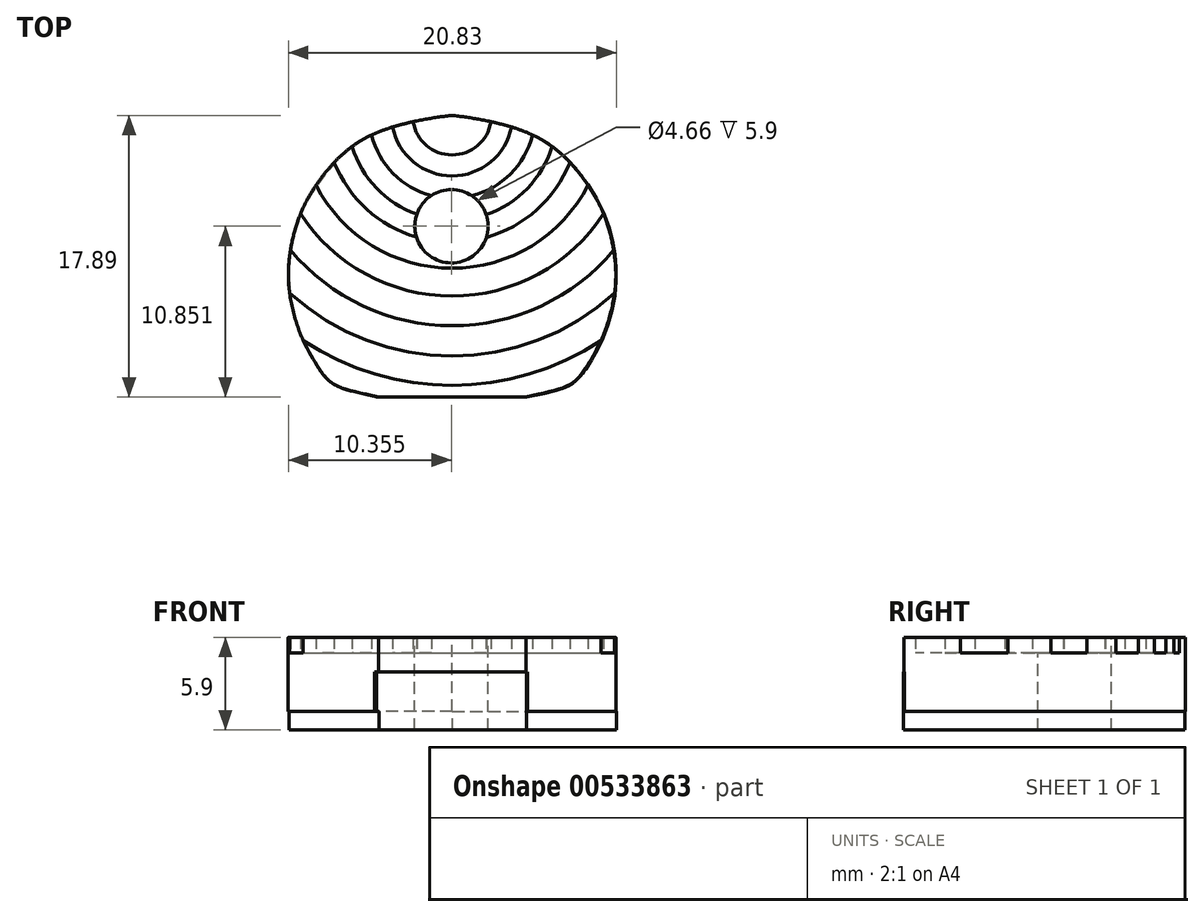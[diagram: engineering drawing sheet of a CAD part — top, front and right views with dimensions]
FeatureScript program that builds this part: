
annotation { "Feature Type Name" : "Feature", "Feature Type Description" : "" }
export const myFeature = defineFeature(function(context is Context, id is Id, definition is map)
    precondition{}
    {
        {
            var Q0;
            Q0=qCreatedBy(makeId("Top.planeOp"),FACE);
            var sketch = newSketch(context, id + "F0", { "sketchPlane" : qUnion([Q0])});
            skLineSegment(sketch, "E0", {"start": v(-18.5, 39.45) * mm, "end": v(-8.99, 39.45) * mm});
            skArc(sketch, "E1", {"start": v(-8.99, 39.45) * mm, "mid": v(-13.75, 56.36) * mm, "end": v(-18.5, 39.45) * mm});
            skLineSegment(sketch, "E2.left", {"start": v(-18.5, 39.45) * mm, "end": v(-18.5, 39.45) * mm});
            skLineSegment(sketch, "E2.right", {"start": v(-8.99, 39.45) * mm, "end": v(-8.99, 39.45) * mm});
            skSolve(sketch);
        }
        {
            var Q0;
            Q0 = qSketchRegion(id + "F0", true);
            extrude(context, id + "F1", {"entities" : qUnion([Q0]), "depth" : 2.5 * mm, "offsetDistance" : 25.4 * mm});
        }
        {
            var Q0;
            Q0=qCreatedBy(makeId("Top.planeOp"),FACE);
            var sketch = newSketch(context, id + "F2", { "sketchPlane" : qUnion([Q0])});
            skCircle(sketch, "E3", {"center": v(-13.67, 50.24) * mm, "radius": 2.3 * mm});
            skSolve(sketch);
        }
        {
            var Q0;
            Q0 = qSketchRegion(id + "F2", true);
            extrude(context, id + "F3", {"entities" : qUnion([Q0]), "operationType" : NewBodyOperationType.REMOVE, "depth" : 25.4 * mm, "offsetDistance" : 25.4 * mm});
        }
        {
            var Q0;
            Q0=qCreatedBy(makeId("Top.planeOp"),FACE);
            var sketch = newSketch(context, id + "F4", { "sketchPlane" : qUnion([Q0])});
            skFitSpline(sketch, "E4", {"points": [v(-13.67, 57.32) * mm, v(-9.2, 56.35) * mm, v(-6.45, 54.6) * mm, v(-4.29, 51.61) * mm, v(-3.41, 48.8) * mm, v(-3.32, 46.28) * mm, v(-4.06, 43.38) * mm, v(-5.02, 41.54) * mm, v(-6.08, 40.3) * mm, v(-8.99, 39.45) * mm], "startDerivative": vector(30, -3) * mm, "endDerivative": vector(-35.55, -8) * mm});
            skFitSpline(sketch, "E5.MirrorCS", {"points": [v(-13.67, 57.32) * mm, v(-18.13, 56.35) * mm, v(-20.9, 54.6) * mm, v(-23.05, 51.61) * mm, v(-23.93, 48.8) * mm, v(-24.02, 46.28) * mm, v(-23.28, 43.38) * mm, v(-22.32, 41.54) * mm, v(-21.26, 40.3) * mm, v(-18.35, 39.45) * mm], "startDerivative": vector(-30, -3) * mm, "endDerivative": vector(35.55, -8) * mm});
            skLineSegment(sketch, "E6", {"start": v(-18.35, 39.45) * mm, "end": v(-8.99, 39.45) * mm});
            skSolve(sketch);
        }
        {
            var Q0;
            Q0 = qSketchRegion(id + "F4", true);
            extrude(context, id + "F5", {"entities" : qUnion([Q0]), "operationType" : NewBodyOperationType.ADD, "oppositeDirection" : true, "depth" : 1.2 * mm, "offsetDistance" : 25.4 * mm});
        }
        {
            var Q0;
            Q0=qCreatedBy(makeId("Top.planeOp"),FACE);
            cPlane(context, id + "F6", {"entities" : qUnion([Q0]), "cplaneType" : CPlaneType.OFFSET, "offset" : 2.5 * mm, "width" : 152.4 * mm, "height" : 152.4 * mm});
        }
        {
            var Q0;
            Q0=qCreatedBy(id+"F6.planeOp",FACE);
            var sketch = newSketch(context, id + "F7", { "sketchPlane" : qUnion([Q0])});
            skFitSpline(sketch, "E7", {"points": [v(-13.7, 57.34) * mm, v(-9.24, 56.37) * mm, v(-6.48, 54.62) * mm, v(-4.32, 51.63) * mm, v(-3.45, 48.83) * mm, v(-3.36, 46.3) * mm, v(-4.1, 43.4) * mm, v(-5.06, 41.56) * mm, v(-6.12, 40.32) * mm, v(-9.02, 39.47) * mm], "startDerivative": vector(30, -3) * mm, "endDerivative": vector(-35.55, -8) * mm});
            skFitSpline(sketch, "E8.MirrorCS", {"points": [v(-13.7, 57.34) * mm, v(-18.17, 56.37) * mm, v(-20.93, 54.62) * mm, v(-23.09, 51.63) * mm, v(-23.96, 48.83) * mm, v(-24.05, 46.3) * mm, v(-23.32, 43.4) * mm, v(-22.35, 41.56) * mm, v(-21.3, 40.32) * mm, v(-18.39, 39.47) * mm], "startDerivative": vector(-30, -3) * mm, "endDerivative": vector(35.55, -8) * mm});
            skLineSegment(sketch, "E9", {"start": v(-18.39, 39.47) * mm, "end": v(-9.02, 39.47) * mm});
            skSolve(sketch);
        }
        {
            var Q0;
            Q0 = qSketchRegion(id + "F7", true);
            extrude(context, id + "F8", {"entities" : qUnion([Q0]), "operationType" : NewBodyOperationType.ADD, "oppositeDirection" : true, "depth" : 2.5 * mm, "offsetDistance" : 25.4 * mm});
        }
        {
            var Q0;
            Q0 = qSketchRegion(id + "F7", true);
            extrude(context, id + "F9", {"entities" : qUnion([Q0]), "operationType" : NewBodyOperationType.ADD, "depth" : 1.2 * mm, "offsetDistance" : 25.4 * mm});
        }
        {
            var Q0;
            Q0=makeQuery(id+"F9.opExtrude","CAP_FACE",FACE,{"disambiguationData":[OSD([sQuery(id+"F7.wireOp",EDGE,"E7"),sQuery(id+"F7.wireOp",EDGE,"E8.MirrorCS"),sQuery(id+"F7.wireOp",EDGE,"E9")])],"isStart":false});
            var sketch = newSketch(context, id + "F10", { "sketchPlane" : qUnion([Q0])});
            skCircle(sketch, "E10", {"center": v(-13.75, 50.3) * mm, "radius": 2.33 * mm});
            skSolve(sketch);
        }
        {
            var Q0;
            Q0 = qSketchRegion(id + "F10", true);
            extrude(context, id + "F11", {"entities" : qUnion([Q0]), "operationType" : NewBodyOperationType.REMOVE, "oppositeDirection" : true, "depth" : 25.4 * mm, "offsetDistance" : 25.4 * mm});
        }
        {
            var Q0;
            Q0=makeQuery(id+"F9.opExtrude","CAP_FACE",FACE,{"disambiguationData":[OSD([sQuery(id+"F7.wireOp",EDGE,"E7"),sQuery(id+"F7.wireOp",EDGE,"E8.MirrorCS"),sQuery(id+"F7.wireOp",EDGE,"E9")])],"isStart":false});
            var sketch = newSketch(context, id + "F12", { "sketchPlane" : qUnion([Q0])});
            skCircle(sketch, "E11", {"center": v(-13.7, 57.34) * mm, "radius": 2.5 * mm});
            skCircle(sketch, "E12", {"center": v(-13.7, 57.34) * mm, "radius": 3.84 * mm});
            skCircle(sketch, "E13", {"center": v(-13.7, 57.34) * mm, "radius": 5.25 * mm});
            skCircle(sketch, "E14", {"center": v(-13.7, 57.34) * mm, "radius": 6.66 * mm});
            skCircle(sketch, "E15", {"center": v(-13.7, 57.34) * mm, "radius": 8.05 * mm});
            skCircle(sketch, "E16", {"center": v(-13.7, 57.34) * mm, "radius": 9.7 * mm});
            skCircle(sketch, "E17", {"center": v(-13.7, 57.34) * mm, "radius": 11.47 * mm});
            skCircle(sketch, "E18", {"center": v(-13.7, 57.34) * mm, "radius": 13.36 * mm});
            skCircle(sketch, "E19", {"center": v(-13.7, 57.34) * mm, "radius": 15.28 * mm});
            skCircle(sketch, "E20", {"center": v(-13.7, 57.34) * mm, "radius": 17.14 * mm});
            skSolve(sketch);
        }
        {
            var Q0;
            {var subQ0=sQuery(id+"F12.wireOp",EDGE,"E11");var subQ1=makeQuery(id+"F9.opExtrude","CAP_EDGE",EDGE,{"disambiguationData":[OSD([sQuery(id+"F7.wireOp",EDGE,"E7")])],"isStart":false});var subQ2=makeQuery(id+"F12.imprint","INTERSECT",VERTEX,{"derivedFrom":[subQ1,subQ0]});Q0=makeQuery(id+"F12.imprint","IMPRINT",FACE,{"disambiguationData":[TD([[makeQuery(id+"F12.imprint","IMPRINT",EDGE,{"disambiguationData":[TD([[subQ2,1.0]])],"derivedFrom":subQ0}),1.0]])]});}
            var Q1;
            {var subQ1=makeQuery(id+"F9.opExtrude","CAP_EDGE",EDGE,{"disambiguationData":[OSD([sQuery(id+"F7.wireOp",EDGE,"E7")])],"isStart":false});var subQ3=sQuery(id+"F12.wireOp",EDGE,"E12");var subQ4=makeQuery(id+"F12.imprint","INTERSECT",VERTEX,{"derivedFrom":[subQ1,subQ3]});Q1=makeQuery(id+"F12.imprint","IMPRINT",FACE,{"disambiguationData":[TD([[makeQuery(id+"F12.imprint","IMPRINT",EDGE,{"disambiguationData":[TD([[subQ4,1.0]])],"derivedFrom":subQ3}),-1.0]])]});}
            var Q2;
            {var subQ0=sQuery(id+"F12.wireOp",EDGE,"E14");var subQ1=makeQuery(id+"F11.boolean.opBoolean","COPY",EDGE,{"derivedFrom":makeQuery(id+"F11.opExtrude","CAP_EDGE",EDGE,{"disambiguationData":[OSD([sQuery(id+"F10.wireOp",EDGE,"E10")])],"isStart":true})});var subQ2=makeQuery(id+"F12.imprint","INTERSECT",VERTEX,{"disambiguationData":[OD(0.0)],"derivedFrom":[subQ1,subQ0]});Q2=makeQuery(id+"F12.imprint","IMPRINT",FACE,{"disambiguationData":[TD([[makeQuery(id+"F12.imprint","IMPRINT",EDGE,{"disambiguationData":[TD([[subQ2,1.0]])],"derivedFrom":subQ0}),-1.0]])]});}
            var Q3;
            {var subQ0=sQuery(id+"F12.wireOp",EDGE,"E14");var subQ1=makeQuery(id+"F11.boolean.opBoolean","COPY",EDGE,{"derivedFrom":makeQuery(id+"F11.opExtrude","CAP_EDGE",EDGE,{"disambiguationData":[OSD([sQuery(id+"F10.wireOp",EDGE,"E10")])],"isStart":true})});var subQ2=makeQuery(id+"F12.imprint","INTERSECT",VERTEX,{"disambiguationData":[OD(1.0)],"derivedFrom":[subQ1,subQ0]});Q3=makeQuery(id+"F12.imprint","IMPRINT",FACE,{"disambiguationData":[TD([[makeQuery(id+"F12.imprint","IMPRINT",EDGE,{"disambiguationData":[TD([[subQ2,-1.0]])],"derivedFrom":subQ0}),-1.0]])]});}
            var Q4;
            {var subQ0=sQuery(id+"F12.wireOp",EDGE,"E16");var subQ1=makeQuery(id+"F9.opExtrude","CAP_EDGE",EDGE,{"disambiguationData":[OSD([sQuery(id+"F7.wireOp",EDGE,"E7")])],"isStart":false});var subQ2=makeQuery(id+"F12.imprint","INTERSECT",VERTEX,{"derivedFrom":[subQ1,subQ0]});Q4=makeQuery(id+"F12.imprint","IMPRINT",FACE,{"disambiguationData":[TD([[makeQuery(id+"F12.imprint","IMPRINT",EDGE,{"disambiguationData":[TD([[subQ2,1.0]])],"derivedFrom":subQ0}),-1.0]])]});}
            var Q5;
            {var subQ0=sQuery(id+"F12.wireOp",EDGE,"E18");var subQ1=makeQuery(id+"F9.opExtrude","CAP_EDGE",EDGE,{"disambiguationData":[OSD([sQuery(id+"F7.wireOp",EDGE,"E7")])],"isStart":false});var subQ2=makeQuery(id+"F12.imprint","INTERSECT",VERTEX,{"derivedFrom":[subQ1,subQ0]});Q5=makeQuery(id+"F12.imprint","IMPRINT",FACE,{"disambiguationData":[TD([[makeQuery(id+"F12.imprint","IMPRINT",EDGE,{"disambiguationData":[TD([[subQ2,1.0]])],"derivedFrom":subQ0}),-1.0]])]});}
            var Q6;
            {var subQ5=makeQuery(id+"F9.opExtrude","CAP_EDGE",EDGE,{"disambiguationData":[OSD([sQuery(id+"F7.wireOp",EDGE,"E9")])],"isStart":false});Q6=makeQuery(id+"F12.imprint","IMPRINT",FACE,{"disambiguationData":[TD([[makeQuery(id+"F12.imprint","IMPRINT",EDGE,{"derivedFrom":subQ5}),1.0]])]});}
            extrude(context, id + "F13", {"entities" : qUnion([Q0, Q1, Q2, Q3, Q4, Q5, Q6]), "operationType" : NewBodyOperationType.ADD, "depth" : 1 * mm, "offsetDistance" : 25.4 * mm});
        }
    });
